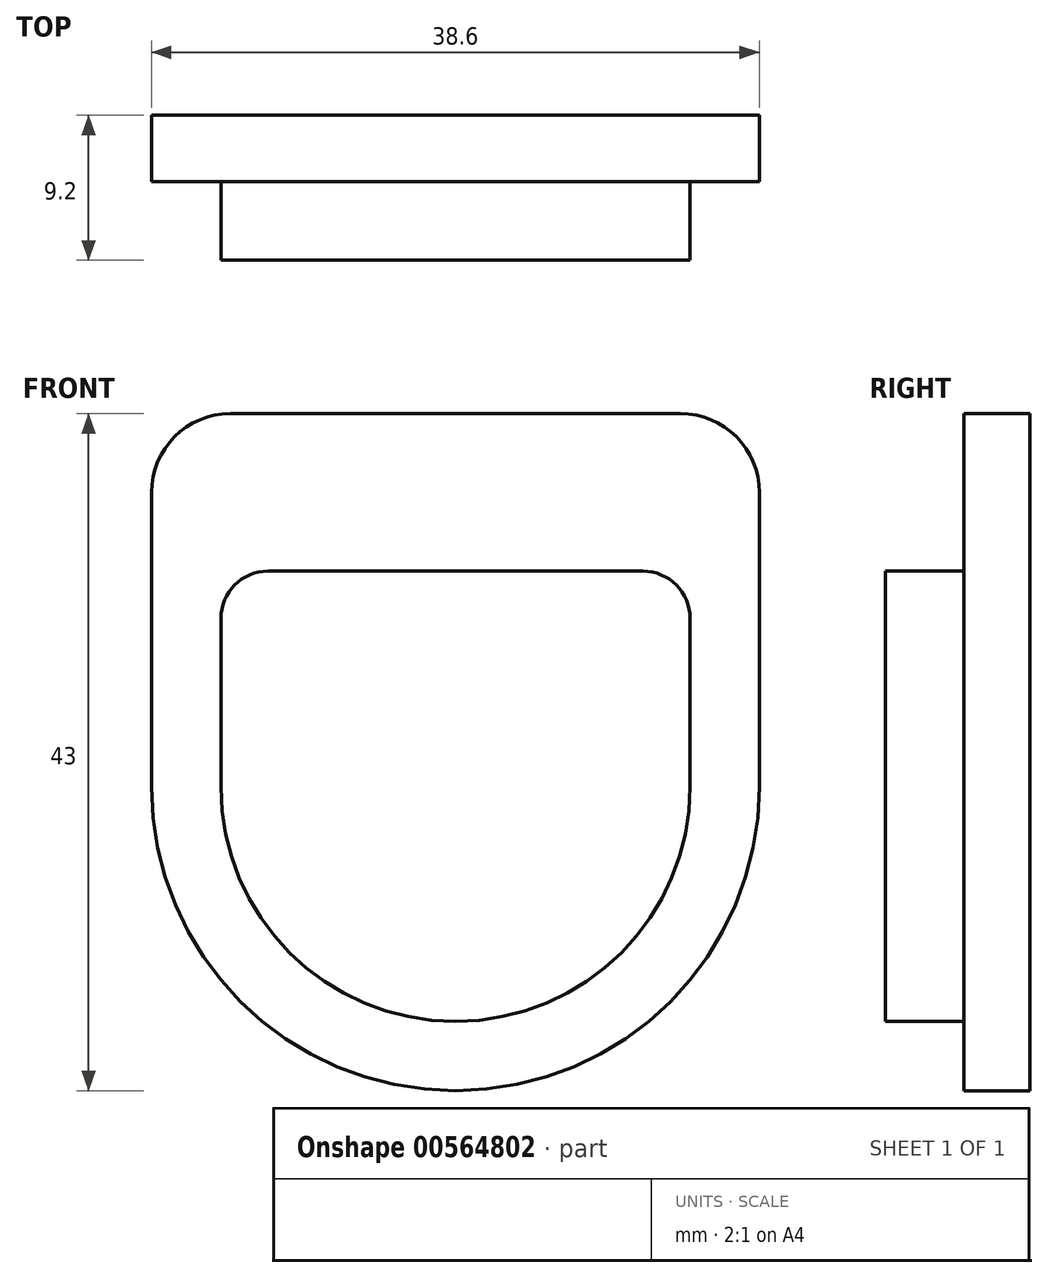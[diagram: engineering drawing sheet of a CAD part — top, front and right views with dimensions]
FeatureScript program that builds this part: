
annotation { "Feature Type Name" : "Feature", "Feature Type Description" : "" }
export const myFeature = defineFeature(function(context is Context, id is Id, definition is map)
    precondition{}
    {
        {
            var Q0;
            Q0=qCreatedBy(makeId("Front.planeOp"),FACE);
            var sketch = newSketch(context, id + "F0", { "sketchPlane" : qUnion([Q0])});
            skArc(sketch, "E0", {"start": v(-19.3, 0) * mm, "mid": v(0, -19.3) * mm, "end": v(19.3, 0) * mm});
            skLineSegment(sketch, "E1.bottom", {"start": v(-19.3, 23.7) * mm, "end": v(19.3, 23.7) * mm});
            skPoint(sketch, "E2", {"position": v(0, 23.7) * mm});
            skPoint(sketch, "E3", {"position": v(-19.3, 0) * mm});
            skPoint(sketch, "E4", {"position": v(19.3, 0) * mm});
            skLineSegment(sketch, "E5", {"start": v(-19.3, 0) * mm, "end": v(-19.3, 13.7) * mm});
            skLineSegment(sketch, "E6", {"start": v(19.3, 0) * mm, "end": v(19.3, 13.7) * mm});
            skLineSegment(sketch, "E7", {"start": v(-19.3, 13.7) * mm, "end": v(-19.3, 23.7) * mm});
            skLineSegment(sketch, "E8", {"start": v(19.3, 13.7) * mm, "end": v(19.3, 23.7) * mm});
            skPoint(sketch, "E1.left.start.orphan", {"position": v(-30, 23.7) * mm});
            skPoint(sketch, "E9.orphan", {"position": v(30, 23.7) * mm});
            skPoint(sketch, "E10", {"position": v(0, -19.3) * mm});
            skSolve(sketch);
        }
        {
            var Q0;
            Q0 = qSketchRegion(id + "F0", true);
            extrude(context, id + "F1", {"entities" : qUnion([Q0]), "oppositeDirection" : true, "depth" : 4.2 * mm, "offsetDistance" : 25 * mm});
        }
        {
            var Q0;
            Q0=qCreatedBy(makeId("Front.planeOp"),FACE);
            var sketch = newSketch(context, id + "F2", { "sketchPlane" : qUnion([Q0])});
            skArc(sketch, "E11", {"start": v(-14.9, 0) * mm, "mid": v(0, -14.9) * mm, "end": v(14.9, 0) * mm});
            skPoint(sketch, "E12", {"position": v(-14.9, 0) * mm});
            skPoint(sketch, "E13", {"position": v(14.9, 0) * mm});
            skLineSegment(sketch, "E14", {"start": v(-14.9, 0) * mm, "end": v(-14.9, 0) * mm});
            skLineSegment(sketch, "E15", {"start": v(14.9, 0) * mm, "end": v(14.9, 0) * mm});
            skLineSegment(sketch, "E16", {"start": v(-14.9, 0) * mm, "end": v(-14.9, 13.7) * mm});
            skLineSegment(sketch, "E17", {"start": v(14.9, 0) * mm, "end": v(14.9, 13.7) * mm});
            skPoint(sketch, "E18", {"position": v(0, -14.9) * mm});
            skLineSegment(sketch, "E19", {"start": v(-14.9, 13.7) * mm, "end": v(14.9, 13.7) * mm});
            skSolve(sketch);
        }
        {
            var Q0;
            Q0 = qSketchRegion(id + "F2", true);
            extrude(context, id + "F3", {"entities" : qUnion([Q0]), "operationType" : NewBodyOperationType.ADD, "depth" : 5 * mm, "offsetDistance" : 25 * mm});
        }
        {
            var Q0;
            Q0=makeQuery(id+"F1.opExtrude","SWEPT_EDGE",EDGE,{"disambiguationData":[OSD([sQuery(id+"F0.wireOp",EDGE,"E1.bottom"),sQuery(id+"F0.wireOp",EDGE,"E7")])]});
            var Q1;
            Q1=makeQuery(id+"F1.opExtrude","SWEPT_EDGE",EDGE,{"disambiguationData":[OSD([sQuery(id+"F0.wireOp",EDGE,"E1.bottom"),sQuery(id+"F0.wireOp",EDGE,"E8")])]});
            fillet(context, id + "F4", {"entities" : qUnion([Q0, Q1]), "radius" : 5 * mm, "tangentPropagation" : true, "allowEdgeOverflow" : false});
        }
        {
            var Q0;
            Q0=makeQuery(id+"F3.opExtrude","SWEPT_EDGE",EDGE,{"disambiguationData":[OSD([sQuery(id+"F2.wireOp",EDGE,"E16"),sQuery(id+"F2.wireOp",EDGE,"E19")])]});
            var Q1;
            Q1=makeQuery(id+"F3.opExtrude","SWEPT_EDGE",EDGE,{"disambiguationData":[OSD([sQuery(id+"F2.wireOp",EDGE,"E17"),sQuery(id+"F2.wireOp",EDGE,"E19")])]});
            fillet(context, id + "F5", {"entities" : qUnion([Q0, Q1]), "radius" : 3 * mm, "tangentPropagation" : true, "allowEdgeOverflow" : false});
        }
    });
